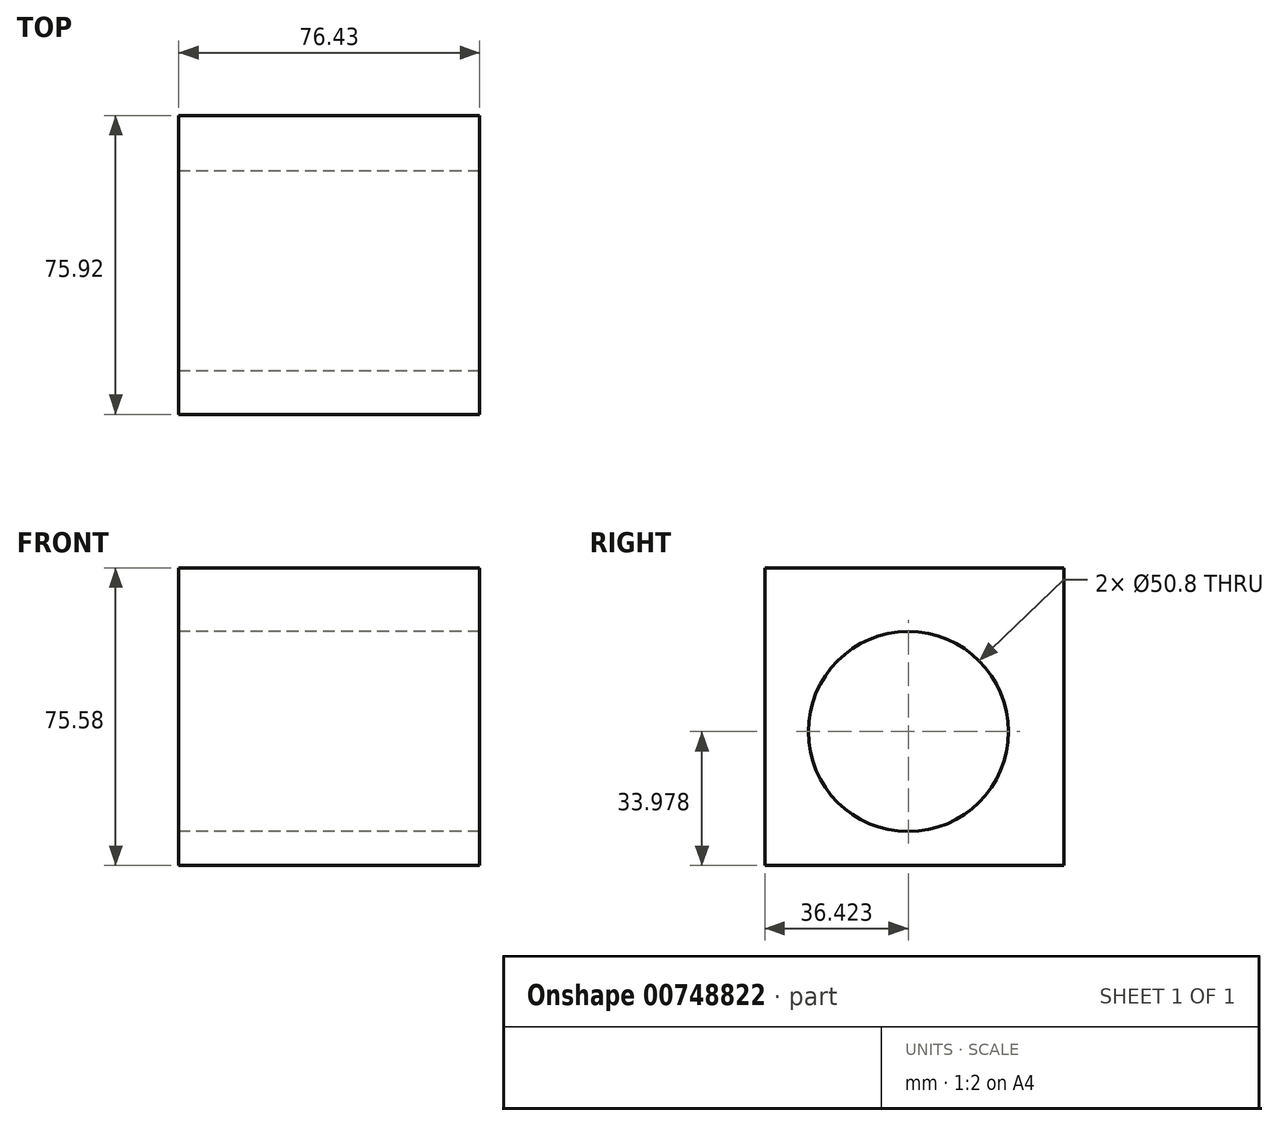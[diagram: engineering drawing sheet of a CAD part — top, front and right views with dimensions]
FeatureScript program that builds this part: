
annotation { "Feature Type Name" : "Feature", "Feature Type Description" : "" }
export const myFeature = defineFeature(function(context is Context, id is Id, definition is map)
    precondition{}
    {
        {
            var Q0;
            Q0=qCreatedBy(makeId("Front.planeOp"),FACE);
            var sketch = newSketch(context, id + "F0", { "sketchPlane" : qUnion([Q0])});
            skLineSegment(sketch, "E0", {"start": v(0, 0) * mm, "end": v(0, -75.58) * mm});
            skLineSegment(sketch, "E1", {"start": v(0, -75.58) * mm, "end": v(76.43, -75.58) * mm});
            skLineSegment(sketch, "E2", {"start": v(76.43, -75.58) * mm, "end": v(76.43, 0) * mm});
            skLineSegment(sketch, "E3", {"start": v(76.43, 0) * mm, "end": v(0, 0) * mm});
            skSolve(sketch);
        }
        {
            var Q0;
            Q0 = qSketchRegion(id + "F0", true);
            extrude(context, id + "F1", {"entities" : qUnion([Q0]), "depth" : 75.92 * mm, "offsetDistance" : 25.4 * mm});
        }
        {
            var Q0;
            Q0=makeQuery(id+"F1.opExtrude","SWEPT_FACE",FACE,{"disambiguationData":[OSD([sQuery(id+"F0.wireOp",EDGE,"E0")])]});
            var sketch = newSketch(context, id + "F2", { "sketchPlane" : qUnion([Q0])});
            skPoint(sketch, "E4", {"position": v(39.5, -41.6) * mm});
            skSolve(sketch);
        }
        {
            var Q0;
            Q0=sQuery(id+"F2.wireOp",VERTEX,"E4");
            var Q1;
            Q1=makeQuery(id+"F1.opExtrude","SWEPT_BODY",BODY,{"disambiguationData":[OSD([sQuery(id+"F0.wireOp",EDGE,"E0"),sQuery(id+"F0.wireOp",EDGE,"E1"),sQuery(id+"F0.wireOp",EDGE,"E2"),sQuery(id+"F0.wireOp",EDGE,"E3")])]});
            hole(context, id + "F3", {"style" : HoleStyle.SIMPLE, "endStyle" : HoleEndStyle.THROUGH, "holeDiameter" : 50.8 * mm, "majorDiameter" : 6.35 * mm, "isTappedThrough" : true, "tappedDepth" : 12.7 * mm, "tapClearance" : 3, "locations" : qUnion([Q0]), "scope" : qUnion([Q1])});
        }
    });
